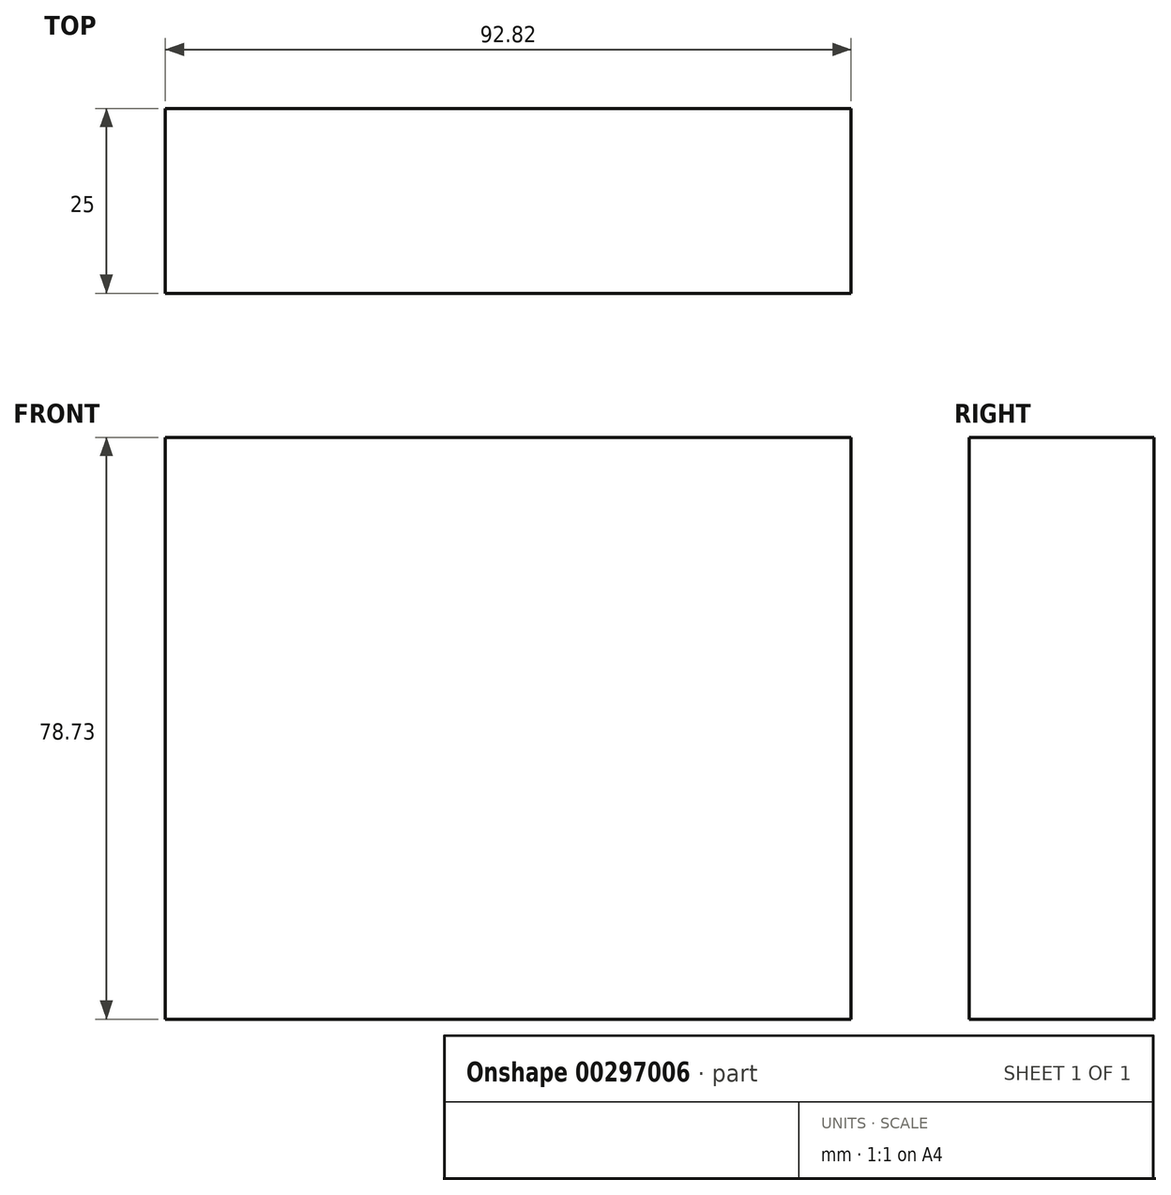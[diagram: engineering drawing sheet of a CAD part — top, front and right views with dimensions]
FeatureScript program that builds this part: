
annotation { "Feature Type Name" : "Feature", "Feature Type Description" : "" }
export const myFeature = defineFeature(function(context is Context, id is Id, definition is map)
    precondition{}
    {
        {
            var Q0;
            Q0=qCreatedBy(makeId("Front.planeOp"),FACE);
            var sketch = newSketch(context, id + "F0", { "sketchPlane" : qUnion([Q0])});
            skLineSegment(sketch, "E0.bottom", {"start": v(-78.54, 10.43) * mm, "end": v(14.28, 10.43) * mm});
            skLineSegment(sketch, "E0.top", {"start": v(-78.54, 89.16) * mm, "end": v(14.28, 89.16) * mm});
            skLineSegment(sketch, "E0.left", {"start": v(-78.54, 10.43) * mm, "end": v(-78.54, 89.16) * mm});
            skLineSegment(sketch, "E0.right", {"start": v(14.28, 10.43) * mm, "end": v(14.28, 89.16) * mm});
            skPoint(sketch, "E0.middle", {"position": v(-32.13, 49.8) * mm});
            skSolve(sketch);
        }
        {
            var Q0;
            Q0=makeQuery(id+"F0.imprint","IMPRINT",FACE,{"disambiguationData":[TD([[makeQuery(id+"F0.imprint","IMPRINT",EDGE,{"derivedFrom":sQuery(id+"F0.wireOp",EDGE,"E0.bottom")}),1.0]])]});
            extrude(context, id + "F1", {"entities" : qUnion([Q0]), "depth" : 25 * mm});
        }
    });
